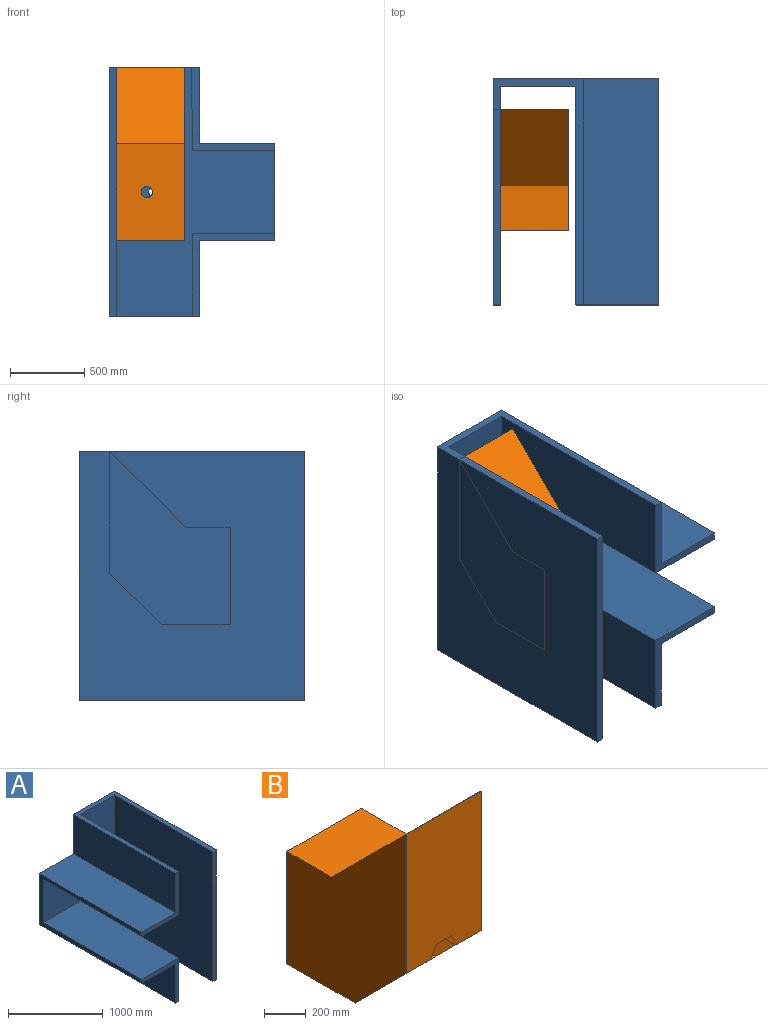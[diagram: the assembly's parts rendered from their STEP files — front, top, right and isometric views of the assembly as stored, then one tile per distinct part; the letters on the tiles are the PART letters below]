
ASSEMBLY  parts=2 mates=2
PART A: 19 faces, bbox 1117.6x1524x1676.4 mm
  f0: plane 558.8x558.8mm, normal (0,-1,0), area 54193.4mm2, adj f4,f5,f8,f9,f13,f14
  f1: plane 1676.4x50.8mm, normal (0,-1,0), area 85161.1mm2, adj f3,f5,f10,f15
  f2: plane 558.8x558.8mm, normal (0,-1,0), area 54193.4mm2, adj f3,f4,f6,f7,f12,f16
  f3: plane 1524x609.6mm, normal (0,0,1), area 180644.8mm2, adj f1,f2,f6,f10,f11,f15,f16,f17
  f4: plane 1524x660.4mm, normal (-1,0,0), area 183225.4mm2, adj f0,f2,f7,f8,f11,f12,f13,f17
  f5: plane 1524x609.6mm, normal (0,0,-1), area 180644.8mm2, adj f0,f1,f9,f10,f11,f14,f15,f17
  f6: plane 1524x508mm, normal (-1,0,0), area 774192mm2, adj f2,f3,f7,f11
  f7: plane 1524x508mm, normal (0,0,1), area 774192mm2, adj f2,f4,f6,f11
  f8: plane 1524x508mm, normal (0,0,-1), area 774192mm2, adj f0,f4,f9,f11
  f9: plane 1524x508mm, normal (-1,0,0), area 774192mm2, adj f0,f5,f8,f11
  f10: plane 1676.4x1524mm, normal (1,0,0), area 2554833.6mm2, adj f1,f3,f5,f11
  f11: plane 1676.4x1117.6mm, normal (0,1,0), area 1352856.3mm2, adj f3,f4,f5,f6,f7,f8,f9,f10
  f12: plane 1473.2x558.8mm, normal (0,0,-1), area 823224.2mm2, adj f2,f4,f16,f17
  f13: plane 1473.2x558.8mm, normal (0,0,1), area 823224.2mm2, adj f0,f4,f14,f17
  f14: plane 1473.2x558.8mm, normal (1,0,0), area 823224.2mm2, adj f0,f5,f13,f17
  f15: plane 1676.4x1473.2mm, normal (-1,0,0), area 2469672.5mm2, adj f1,f3,f5,f17
  f16: plane 1473.2x558.8mm, normal (1,0,0), area 823224.2mm2, adj f2,f3,f12,f17
  f17: plane 1676.4x1066.8mm, normal (0,-1,0), area 1159308.3mm2, adj f3,f4,f5,f12,f13,f14,f15,f16
  f18: cylinder r=38.1mm len=76.2mm, axis (0,1,0), area 12161mm2, adj f11,f17
PART B: 17 faces, bbox 508x812.8x1168.4 mm
  f0: plane 508x1.69mm, normal (0,0,1), area 859.6mm2, adj f1,f3,f4,f7
  f1: plane 1168.4x812.8mm, normal (-1,0,0), area 605635.4mm2, adj f0,f2,f4,f5,f6,f7,f15
  f2: plane 508x463.43mm, normal (0,0,-1), area 235423mm2, adj f1,f3,f5,f15
  f3: plane 1168.4x812.8mm, normal (1,0,0), area 605635.4mm2, adj f0,f2,f4,f5,f6,f7,f15
  f4: plane 819.03x508mm, normal (0,-1,0), area 406341.4mm2, adj f0,f1,f3,f5,f11,f12,f13
  f5: plane 508x349.37mm, normal (0,-0.71,-0.71), area 226821.5mm2, adj f1,f2,f3,f4,f8,f9,f10,f11
  f6: plane 508x303.11mm, normal (0,0,1), area 153978.8mm2, adj f1,f3,f7,f15
  f7: plane 508x508mm, normal (0,0.71,0.71), area 364957.6mm2, adj f0,f1,f3,f6
  f8: plane 742.83x87.99mm, normal (-0.87,0,0.5), area 71001.8mm2, adj f5,f9,f13,f16
  f9: plane 654.84x101.6mm, normal (0,0,1), area 66532mm2, adj f5,f8,f10,f16
  f10: plane 742.83x87.99mm, normal (0.87,0,0.5), area 71001.8mm2, adj f5,f9,f11,f16
  f11: plane 762x87.99mm, normal (0.87,0,-0.5), area 77207.1mm2, adj f4,f5,f10,f12,f16
  f12: plane 762x101.6mm, normal (0,0,-1), area 77419.2mm2, adj f4,f11,f13,f16
  f13: plane 762x87.99mm, normal (-0.87,0,-0.5), area 77207.1mm2, adj f4,f5,f8,f12,f16
  f14: cylinder r=38.1mm len=76.2mm, axis (0,-1,0), area 12161mm2, adj f15,f16
  f15: plane 660.4x508mm, normal (0,1,0), area 330922.8mm2, adj f1,f2,f3,f6,f14
  f16: plane 203.2x175.98mm, normal (0,-1,0), area 22258.4mm2, adj f8,f9,f10,f11,f12,f13,f14
PLACE A rot(axis=(0,1,0),180deg) t=(-205.57,813.45,702.01)mm
PLACE B rot(axis=(0,0,1),180deg) t=(-690.83,-154.86,53.31)mm
MATE planar B.f2 <-> A.f7  axis (0,0,-1) through (-979.38,26.05,43.48)mm
MATE planar B.f3 <-> A.f10  axis (-1,0,0) through (-1233.38,222.24,502.47)mm
